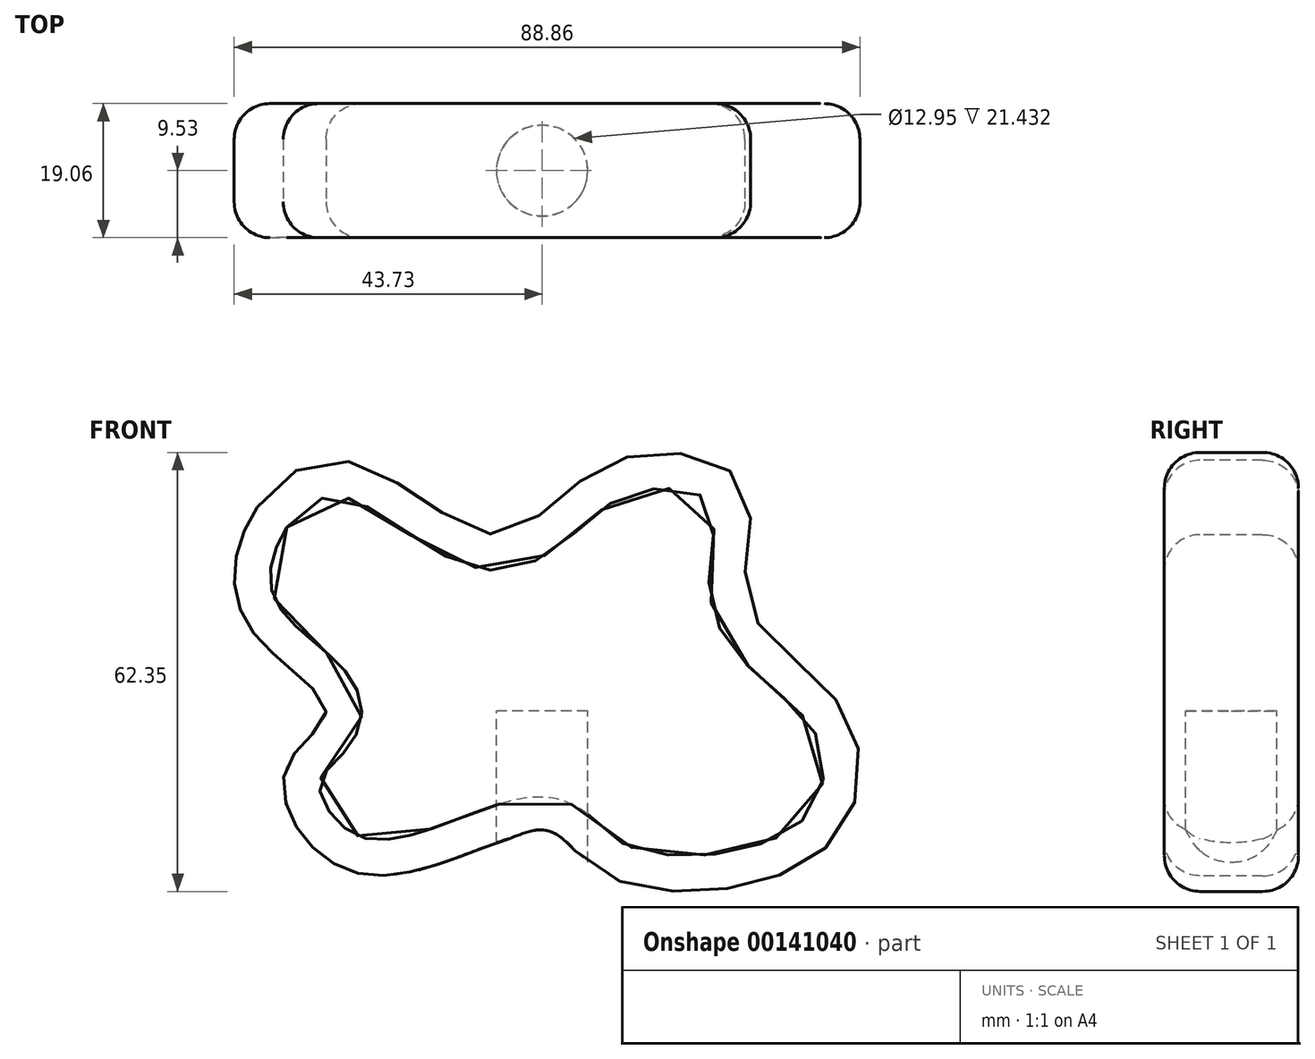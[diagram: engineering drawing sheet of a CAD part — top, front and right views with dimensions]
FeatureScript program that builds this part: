
annotation { "Feature Type Name" : "Feature", "Feature Type Description" : "" }
export const myFeature = defineFeature(function(context is Context, id is Id, definition is map)
    precondition{}
    {
        {
            var Q0;
            Q0=qCreatedBy(makeId("Front.planeOp"),FACE);
            var sketch = newSketch(context, id + "F0", { "sketchPlane" : qUnion([Q0])});
            skFitSpline(sketch, "E0", {"points": [v(-40.42, 28.98) * mm, v(-26.78, 35.3) * mm, v(-6.33, 25.08) * mm, v(9.74, 35.3) * mm, v(28.73, 31.9) * mm, v(29.22, 15.34) * mm, v(42.85, 0) * mm, v(39.93, -19.72) * mm, v(9.74, -23.62) * mm, v(0, -17.29) * mm, v(-25.81, -23.13) * mm, v(-36.52, -8.52) * mm, v(-30.68, 0) * mm, v(-41.88, 12.42) * mm, v(-40.42, 28.98) * mm]});
            skSolve(sketch);
        }
        {
            var Q0;
            Q0 = qSketchRegion(id + "F0", true);
            extrude(context, id + "F1", {"entities" : qUnion([Q0]), "endBound" : BoundingType.SYMMETRIC, "depth" : 19.05 * mm});
        }
        {
            var Q0;
            Q0=qCreatedBy(makeId("Top.planeOp"),FACE);
            var sketch = newSketch(context, id + "F2", { "sketchPlane" : qUnion([Q0])});
            skCircle(sketch, "E1", {"center": v(0, 0) * mm, "radius": 6.48 * mm});
            skSolve(sketch);
        }
        {
            var Q0;
            Q0 = qSketchRegion(id + "F2", true);
            var Q1;
            Q1=makeQuery(id+"F1.opExtrude","SWEPT_FACE",FACE,{"disambiguationData":[OSD([sQuery(id+"F0.wireOp",EDGE,"E0")])]});
            extrude(context, id + "F3", {"entities" : qUnion([Q0]), "operationType" : NewBodyOperationType.REMOVE, "endBound" : BoundingType.UP_TO_SURFACE, "oppositeDirection" : true, "endBoundEntityFace" : qUnion([Q1]), "depth" : 12.7 * mm});
        }
        {
            var Q0;
            Q0=makeQuery(id+"F1.opExtrude","CAP_EDGE",EDGE,{"disambiguationData":[OSD([sQuery(id+"F0.wireOp",EDGE,"E0")])],"isStart":false});
            var Q1;
            Q1=makeQuery(id+"F1.opExtrude","CAP_EDGE",EDGE,{"disambiguationData":[OSD([sQuery(id+"F0.wireOp",EDGE,"E0")])],"isStart":true});
            fillet(context, id + "F4", {"entities" : qUnion([Q0, Q1]), "radius" : 5.08 * mm, "tangentPropagation" : true, "allowEdgeOverflow" : false});
        }
    });
